# Revit family: Edelstahlrohrschelle V4A, M 8, Ø 15- 45, Gummi
name_source: partatom
category: HLS-Bauteile
revit_build: Autodesk Revit 2017 (Build: 20190507_1515(x64)
units: mm (PartAtom-declared; Revit-internal decimal feet)

## family parameters
Arbeitsebenenbasiert = Ja
Beim Laden mit Abzugskörper schneiden = Nein
Bemaßung runder Anschluss = Durchmesser verwenden
Gemeinsam genutzt = Ja
Immer vertikal = Nein
Raumberechnungspunkt = Nein
Teiletyp = Normal

## types (6) — shared parameters
A = 12 mm  [stored 0.0393701 ft]
Anschluss = M8
Anschlußhöhe = 11 mm
Bauart = zweiteilig
Baustoffklasse = B2
DF1 = 13 mm
DS = 4 mm  [stored 0.0131234 ft]
DVS = 7 mm  [stored 0.0229659 ft]
Dämmstärke = 4 mm  [stored 0.0131234 ft]
Fabrikat = MEFA
Farbe Schalldämmeinlage = schwarz
Firma = MEFA Befestigungs- und Montagesysteme GmbH
HGA = 7 mm  [stored 0.0229659 ft]
Kurztext1 = Rohrschelle Edelstahl V4A 20x1,5
MB = 20 mm  [stored 0.0656168 ft]
MD = 2 mm  [stored 0.00656168 ft]
Material = Edelstahl
Material Schalldämmeinlage = TPE
Materialmaße = 20x1,5 mm
Mengeneinheit = St
Schalldämmeinlage = Gummi
Verschluss = Schraubenverschluss
Verschluss-Schraube = M6
Vorgabe-Ansicht = 1219 mm
max. Temperaturbeständigkeit = 100 °C
max. zul. Last horizontal = 0.00 kN
max. zul. Last vertikal = 0.00 kN
vpe = 50 St
zero-valued in all types: Nennweite DN Rohr, Rohraußendurchmesser, Stärke Material

## per-type parameters (varying)
| type | AB | Achsabstand | Artikelnummer | B | D | D0 | DF2 | Dmax | Dmin | EAN | Gewicht | Gewicht pro Bauteil | H | Kurztext2 | R | RM | Rohraußendurchmesser Zoll | S | max. Rohraußendurchmesser | min. Rohraußendurchmesser |
| Edelstahlrohrschelle V4A, M 8, Ø 15- 20, Gummi | 5 mm  [stored 0.0164042 ft] | 43 mm | 0498174 | 56 mm | 20 mm  [stored 0.0656168 ft] | 27 mm  [stored 0.0885827 ft] | 13 mm | 20 mm  [stored 0.0656168 ft] | 15 mm  [stored 0.0492126 ft] | 4250928413772 | 0.06 kg | 0.06 kg | 37 mm | 15 - 20 mm M8 TPE | 14 mm  [stored 0.0459318 ft] | 15 mm  [stored 0.0492126 ft] | 3/8 Zoll | 43 mm  [stored 0.141076 ft] | 20 mm  [stored 0.0656168 ft] | 15 mm  [stored 0.0492126 ft] |
| Edelstahlrohrschelle V4A, M 8, Ø 21- 25, Gummi | 4 mm  [stored 0.0131234 ft] | 48 mm | 0498175 | 61 mm | 25 mm  [stored 0.082021 ft] | 32 mm  [stored 0.104987 ft] | 13 mm | 25 mm  [stored 0.082021 ft] | 21 mm  [stored 0.0688976 ft] | 4250928413789 | 0.06 kg | 0.06 kg | 42 mm | 21 - 25 mm M8 TPE | 16 mm  [stored 0.0524934 ft] | 18 mm  [stored 0.0590551 ft] | 1/2 Zoll | 48 mm  [stored 0.15748 ft] | 25 mm  [stored 0.082021 ft] | 21 mm  [stored 0.0688976 ft] |
| Edelstahlrohrschelle V4A, M 8, Ø 26- 30, Gummi | 4 mm  [stored 0.0131234 ft] | 53 mm | 0498176 | 66 mm | 30 mm  [stored 0.0984252 ft] | 37 mm | 13 mm | 30 mm  [stored 0.0984252 ft] | 26 mm  [stored 0.0853018 ft] | 4250928413796 | 0.07 kg | 0.07 kg | 47 mm  [stored 0.154199 ft] | 26 - 30 mm M8 TPE | 19 mm | 20 mm  [stored 0.0656168 ft] | 3/4 Zoll | 53 mm  [stored 0.173885 ft] | 30 mm  [stored 0.0984252 ft] | 26 mm  [stored 0.0853018 ft] |
| Edelstahlrohrschelle V4A, M 8, Ø 31- 34, Gummi | 3 mm  [stored 0.00984252 ft] | 59 mm | 0498177 | 72 mm | 34 mm | 41 mm  [stored 0.134514 ft] | 15 mm  [stored 0.0492126 ft] | 34 mm | 31 mm  [stored 0.101706 ft] | 4250928413802 | 0.07 kg | 0.07 kg | 51 mm | 31 - 34 mm M8 TPE | 21 mm  [stored 0.0688976 ft] | 22 mm | 1 Zoll | 59 mm | 34 mm | 31 mm  [stored 0.101706 ft] |
| Edelstahlrohrschelle V4A, M 8, Ø 35- 40, Gummi | 5 mm  [stored 0.0164042 ft] | 65 mm | 0498178 | 78 mm | 40 mm  [stored 0.131234 ft] | 47 mm  [stored 0.154199 ft] | 15 mm  [stored 0.0492126 ft] | 40 mm  [stored 0.131234 ft] | 35 mm  [stored 0.114829 ft] | 4250928413819 | 0.08 kg | 0.08 kg | 57 mm | 35 - 40 mm M8 TPE | 24 mm  [stored 0.0787402 ft] | 25 mm  [stored 0.082021 ft] | Zoll | 65 mm | 40 mm  [stored 0.131234 ft] | 35 mm  [stored 0.114829 ft] |
| Edelstahlrohrschelle V4A, M 8, Ø 41- 45, Gummi | 4 mm  [stored 0.0131234 ft] | 7 mm | 0498179 | 83 mm | 45 mm  [stored 0.147638 ft] | 52 mm  [stored 0.170604 ft] | 15 mm  [stored 0.0492126 ft] | 45 mm  [stored 0.147638 ft] | 41 mm  [stored 0.134514 ft] | 4250928413826 | 0.08 kg | 0.08 kg | 62 mm | 41 - 45 mm M8 TPE | 26 mm  [stored 0.0853018 ft] | 28 mm | 1 1/4 Zoll | 70 mm | 45 mm  [stored 0.147638 ft] | 41 mm  [stored 0.134514 ft] |

note: [stored X ft] marks values corroborated as IEEE doubles in the binary element streams (Revit-internal decimal feet)

## geometry (parser evidence)
native form markers: Sweep x6
no freeform markers — native parametric forms only
